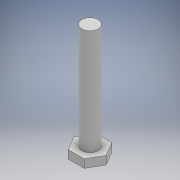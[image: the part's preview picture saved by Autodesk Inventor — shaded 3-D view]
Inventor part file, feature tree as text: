
AUTODESK INVENTOR PART (.ipt)
format: ipt  version: 2018.3 (Build 223284000, 284)  size: 102,912 bytes
history: native  units: mm
features: extrude x2, sketch x2, other x1
ambient origin geometry x8: Origin, YZ Plane, XZ Plane, XY Plane, X Axis, Y Axis, Z Axis, Center Point
bodies: Body1 (feature_tree)
feature tree (5):
  other  "Sólido1"
  extrude  "Extrusión1"  Depth=1.5mm
  extrude  "Extrusión2"  [1 undecoded]
  sketch  "Boceto1"  dims[d1=1.5mm d2=0.0mm d3=2.9mm]
  sketch  "Boceto2"  dims[d4=19.0mm d5=0.0mm]
note: 1 required parameter value undecoded (feature->parameter linkage not recoverable at this tier; creation-order binding heuristic only, values carry confidence <= 0.55)
